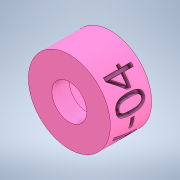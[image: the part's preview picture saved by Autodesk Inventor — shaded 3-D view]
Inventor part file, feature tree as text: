
AUTODESK INVENTOR PART (.ipt)
format: ipt  version: 2021.1 (Build 251245000, 245)  size: 243,200 bytes
history: native  units: in
note: dims shown in document units (in); Inventor stores cm internally (conversion verified against a paired STEP export)
features: sketch x3, extrude x1, revolve x1, plane x1, emboss x1
ambient origin geometry x8: Origin, YZ Plane, XZ Plane, XY Plane, X Axis, Y Axis, Z Axis, Center Point
bodies: Solid1 (feature_tree)
feature tree (7):
  extrude  "Extrusion1"  Depth=1.49in
  revolve  "Revolution1"  Angle=30.0deg
  plane  "Work Plane1"
  emboss  "Emboss1"
  sketch  "Sketch1"  dims[d0=0.635in d1=1.49in]
  sketch  "Sketch3"  dims[d2=0.75in d3=0.0in d8=30.0deg]
  sketch  "Sketch9"  dims[d9=90.0deg d10=0.25in d36=0.745in d37=0.1in d38=0.0in d28=0.5in d29=0.0344in d30=0.5in d31=0.0344in]
